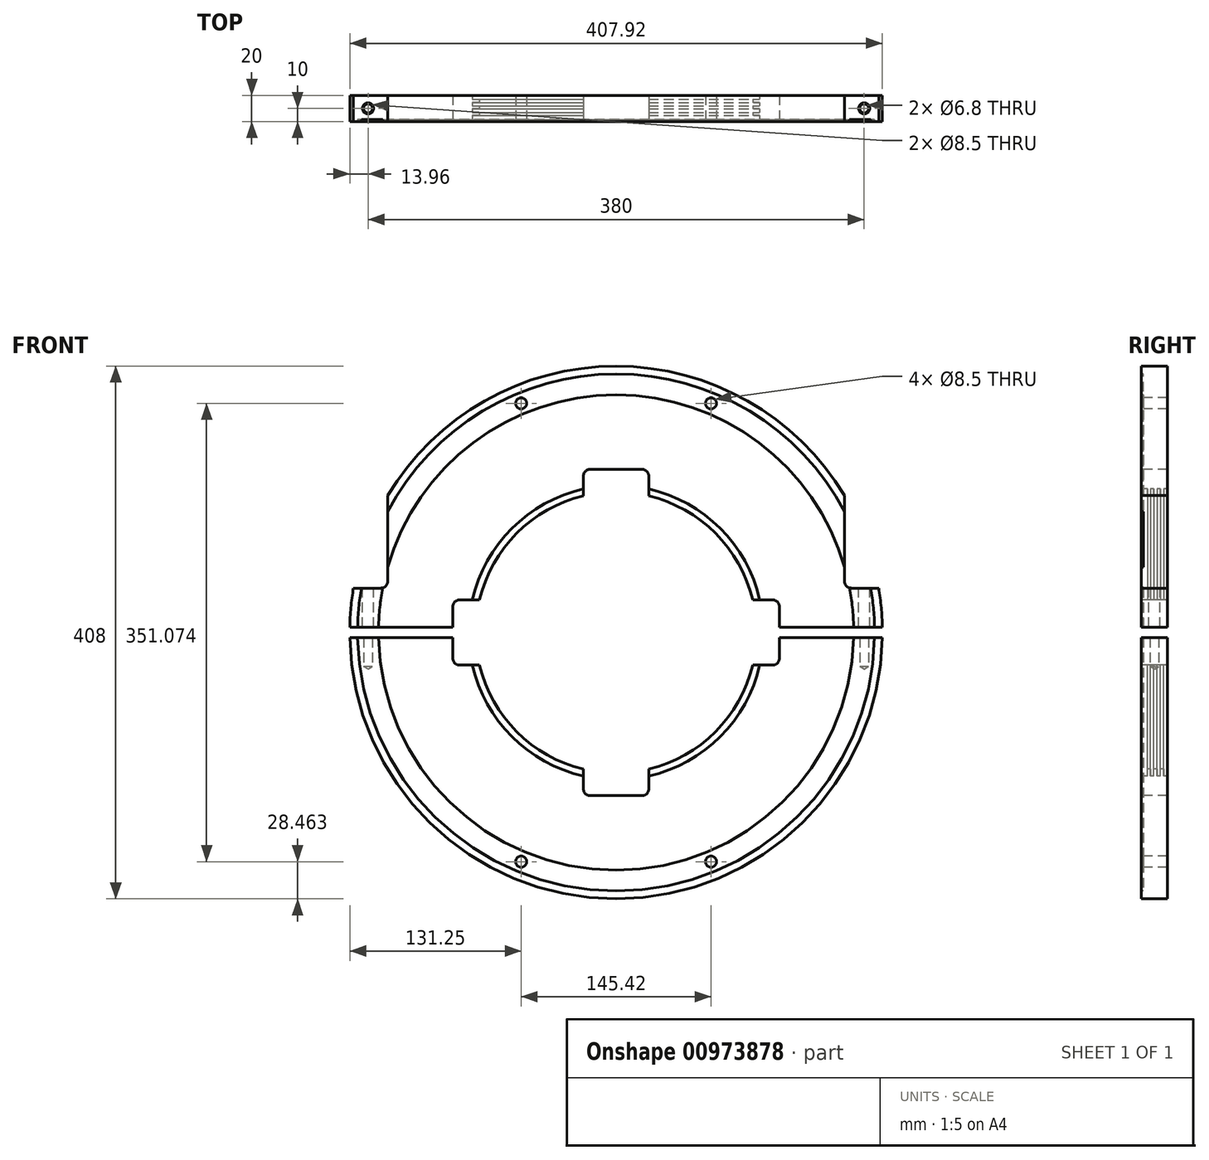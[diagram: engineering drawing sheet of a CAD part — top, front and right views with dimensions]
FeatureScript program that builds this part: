
annotation { "Feature Type Name" : "Feature", "Feature Type Description" : "" }
export const myFeature = defineFeature(function(context is Context, id is Id, definition is map)
    precondition{}
    {
        {
            var Q0;
            Q0=qCreatedBy(makeId("Right.planeOp"),FACE);
            var sketch = newSketch(context, id + "F0", { "sketchPlane" : qUnion([Q0])});
            skLineSegment(sketch, "E0", {"start": v(0, 204) * mm, "end": v(20, 204) * mm});
            skLineSegment(sketch, "E1", {"start": v(0, 204) * mm, "end": v(0, 198) * mm});
            skLineSegment(sketch, "E2", {"start": v(0, 198) * mm, "end": v(1.5, 198) * mm});
            skLineSegment(sketch, "E3", {"start": v(1.5, 198) * mm, "end": v(1.5, 182) * mm});
            skLineSegment(sketch, "E4", {"start": v(1.5, 182) * mm, "end": v(0, 182) * mm});
            skLineSegment(sketch, "E5", {"start": v(0, 182) * mm, "end": v(0, 112.8) * mm});
            skLineSegment(sketch, "E6", {"start": v(0, 112.8) * mm, "end": v(4.6, 112.8) * mm});
            skLineSegment(sketch, "E7", {"start": v(4.6, 112.8) * mm, "end": v(4.6, 107.6) * mm});
            skLineSegment(sketch, "E8", {"start": v(4.6, 107.6) * mm, "end": v(7, 107.6) * mm});
            skLineSegment(sketch, "E9", {"start": v(7, 107.6) * mm, "end": v(7, 112.8) * mm});
            skLineSegment(sketch, "E10", {"start": v(7, 112.8) * mm, "end": v(9.6, 112.8) * mm});
            skLineSegment(sketch, "E11", {"start": v(9.6, 112.8) * mm, "end": v(9.6, 107.6) * mm});
            skLineSegment(sketch, "E12", {"start": v(9.6, 107.6) * mm, "end": v(12, 107.6) * mm});
            skLineSegment(sketch, "E13", {"start": v(12, 107.6) * mm, "end": v(12, 112.8) * mm});
            skLineSegment(sketch, "E14", {"start": v(12, 112.8) * mm, "end": v(14.6, 112.8) * mm});
            skLineSegment(sketch, "E15", {"start": v(14.6, 112.8) * mm, "end": v(14.6, 107.6) * mm});
            skLineSegment(sketch, "E16", {"start": v(14.6, 107.6) * mm, "end": v(17, 107.6) * mm});
            skLineSegment(sketch, "E17", {"start": v(17, 107.6) * mm, "end": v(17, 112.8) * mm});
            skLineSegment(sketch, "E18", {"start": v(17, 112.8) * mm, "end": v(20, 112.8) * mm});
            skLineSegment(sketch, "E19", {"start": v(20, 204) * mm, "end": v(20, 112.8) * mm});
            skPoint(sketch, "E20.orphan", {"position": v(0, 107.6) * mm});
            skLineSegment(sketch, "E21", {"start": v(0, 0) * mm, "end": v(20, 0) * mm, "construction": true});
            skSolve(sketch);
        }
        {
            var Q0;
            Q0 = qSketchRegion(id + "F0", true);
            var Q1;
            Q1=sQuery(id+"F0.wireOp",EDGE,"E21");
            revolve(context, id + "F1", {"surfaceOperationType" : NewSurfaceOperationType.NEW, "entities" : qUnion([Q0]), "axis" : qUnion([Q1]), "revolveType" : RevolveType.FULL});
        }
        {
            var Q0;
            Q0=qCreatedBy(makeId("Front.planeOp"),FACE);
            var sketch = newSketch(context, id + "F2", { "sketchPlane" : qUnion([Q0])});
            skLineSegment(sketch, "E22.bottom", {"start": v(-204, 4) * mm, "end": v(204, 4) * mm});
            skLineSegment(sketch, "E22.top", {"start": v(-204, -4) * mm, "end": v(204, -4) * mm});
            skLineSegment(sketch, "E22.left", {"start": v(-204, 4) * mm, "end": v(-204, -4) * mm});
            skLineSegment(sketch, "E22.right", {"start": v(204, 4) * mm, "end": v(204, -4) * mm});
            skLineSegment(sketch, "E23.bottom", {"start": v(-255, 34) * mm, "end": v(-175, 34) * mm});
            skLineSegment(sketch, "E23.top", {"start": v(-255, 114) * mm, "end": v(-175, 114) * mm});
            skLineSegment(sketch, "E23.left", {"start": v(-255, 34) * mm, "end": v(-255, 114) * mm});
            skLineSegment(sketch, "E23.right", {"start": v(-175, 34) * mm, "end": v(-175, 114) * mm});
            skLineSegment(sketch, "E24.bottom", {"start": v(255, 34) * mm, "end": v(175, 34) * mm});
            skLineSegment(sketch, "E24.top", {"start": v(255, 114) * mm, "end": v(175, 114) * mm});
            skLineSegment(sketch, "E24.left", {"start": v(255, 34) * mm, "end": v(255, 114) * mm});
            skLineSegment(sketch, "E24.right", {"start": v(175, 34) * mm, "end": v(175, 114) * mm});
            skCircle(sketch, "E25", {"center": v(0, 0) * mm, "radius": 190 * mm, "construction": true});
            skLineSegment(sketch, "E26", {"start": v(0, 0) * mm, "end": v(-72.7, 175.54) * mm, "construction": true});
            skLineSegment(sketch, "E27", {"start": v(0, 0) * mm, "end": v(72.7, 175.54) * mm, "construction": true});
            skLineSegment(sketch, "E28", {"start": v(0, 0) * mm, "end": v(-72.7, -175.54) * mm, "construction": true});
            skLineSegment(sketch, "E29", {"start": v(0, 0) * mm, "end": v(72.7, -175.54) * mm, "construction": true});
            skCircle(sketch, "E30", {"center": v(-72.7, 175.54) * mm, "radius": 4.25 * mm});
            skCircle(sketch, "E31", {"center": v(72.7, 175.54) * mm, "radius": 4.25 * mm});
            skCircle(sketch, "E32", {"center": v(-72.7, -175.54) * mm, "radius": 4.25 * mm});
            skCircle(sketch, "E33", {"center": v(72.7, -175.54) * mm, "radius": 4.25 * mm});
            skLineSegment(sketch, "E34.bottom", {"start": v(-25, 125) * mm, "end": v(25, 125) * mm});
            skLineSegment(sketch, "E34.top", {"start": v(-25, -125) * mm, "end": v(25, -125) * mm});
            skLineSegment(sketch, "E34.left", {"start": v(-25, 125) * mm, "end": v(-25, -125) * mm});
            skLineSegment(sketch, "E34.right", {"start": v(25, 125) * mm, "end": v(25, -125) * mm});
            skLineSegment(sketch, "E35.bottom", {"start": v(-125, -25) * mm, "end": v(125, -25) * mm});
            skLineSegment(sketch, "E35.top", {"start": v(-125, 25) * mm, "end": v(125, 25) * mm});
            skLineSegment(sketch, "E35.left", {"start": v(-125, -25) * mm, "end": v(-125, 25) * mm});
            skLineSegment(sketch, "E35.right", {"start": v(125, -25) * mm, "end": v(125, 25) * mm});
            skSolve(sketch);
        }
        {
            var Q0;
            Q0 = qSketchRegion(id + "F2", true);
            extrude(context, id + "F3", {"entities" : qUnion([Q0]), "operationType" : NewBodyOperationType.REMOVE, "oppositeDirection" : true, "depth" : 25 * mm, "offsetDistance" : 25 * mm});
        }
        {
            var Q0;
            Q0=qCreatedBy(makeId("Top.planeOp"),FACE);
            var sketch = newSketch(context, id + "F4", { "sketchPlane" : qUnion([Q0])});
            skLineSegment(sketch, "E36", {"start": v(-190, 10) * mm, "end": v(190, 10) * mm, "construction": true});
            skSolve(sketch);
        }
        {
            var Q0;
            Q0=sQuery(id+"F4.wireOp",VERTEX,"E36.start");
            var Q1;
            Q1=sQuery(id+"F4.wireOp",VERTEX,"E36.end");
            var Q2;
            Q2=makeQuery(id+"F3.boolean.opBoolean","SPLIT",BODY,{"disambiguationData":[OD(0.0)],"derivedFrom":makeQuery(id+"F1.opRevolve","SWEPT_BODY",BODY,{"disambiguationData":[OSD([sQuery(id+"F0.wireOp",EDGE,"E0"),sQuery(id+"F0.wireOp",EDGE,"E1"),sQuery(id+"F0.wireOp",EDGE,"E2"),sQuery(id+"F0.wireOp",EDGE,"E3"),sQuery(id+"F0.wireOp",EDGE,"E4"),sQuery(id+"F0.wireOp",EDGE,"E5"),sQuery(id+"F0.wireOp",EDGE,"E6"),sQuery(id+"F0.wireOp",EDGE,"E7"),sQuery(id+"F0.wireOp",EDGE,"E8"),sQuery(id+"F0.wireOp",EDGE,"E9"),sQuery(id+"F0.wireOp",EDGE,"E10"),sQuery(id+"F0.wireOp",EDGE,"E11"),sQuery(id+"F0.wireOp",EDGE,"E12"),sQuery(id+"F0.wireOp",EDGE,"E13"),sQuery(id+"F0.wireOp",EDGE,"E14"),sQuery(id+"F0.wireOp",EDGE,"E15"),sQuery(id+"F0.wireOp",EDGE,"E16"),sQuery(id+"F0.wireOp",EDGE,"E17"),sQuery(id+"F0.wireOp",EDGE,"E18"),sQuery(id+"F0.wireOp",EDGE,"E19")])]})});
            hole(context, id + "F5", {"style" : HoleStyle.SIMPLE, "endStyle" : HoleEndStyle.BLIND, "standardTappedOrClearance" : lookupTablePath({ "standard" : "ISO", "engagement" : "75%", "pitch" : "1.25 mm", "size" : "M8", "type" : "Tapped" }), "standardBlindInLast" : lookupTablePath({ "standard" : "ISO", "fit" : "Normal", "engagement" : "75%", "pitch" : "1.25 mm", "size" : "M8", "type" : "Clearance & tapped" }), "holeDiameter" : 6.8 * mm, "majorDiameter" : 8 * mm, "showTappedDepth" : true, "holeDepth" : 22 * mm, "tappedDepth" : 17 * mm, "tapClearance" : 4, "locations" : qUnion([Q0, Q1]), "scope" : qUnion([Q2])});
        }
        {
            var Q0;
            Q0=sQuery(id+"F4.wireOp",VERTEX,"E36.start");
            var Q1;
            Q1=sQuery(id+"F4.wireOp",VERTEX,"E36.end");
            var Q2;
            Q2=makeQuery(id+"F3.boolean.opBoolean","SPLIT",BODY,{"disambiguationData":[OD(1.0)],"derivedFrom":makeQuery(id+"F1.opRevolve","SWEPT_BODY",BODY,{"disambiguationData":[OSD([sQuery(id+"F0.wireOp",EDGE,"E0"),sQuery(id+"F0.wireOp",EDGE,"E1"),sQuery(id+"F0.wireOp",EDGE,"E2"),sQuery(id+"F0.wireOp",EDGE,"E3"),sQuery(id+"F0.wireOp",EDGE,"E4"),sQuery(id+"F0.wireOp",EDGE,"E5"),sQuery(id+"F0.wireOp",EDGE,"E6"),sQuery(id+"F0.wireOp",EDGE,"E7"),sQuery(id+"F0.wireOp",EDGE,"E8"),sQuery(id+"F0.wireOp",EDGE,"E9"),sQuery(id+"F0.wireOp",EDGE,"E10"),sQuery(id+"F0.wireOp",EDGE,"E11"),sQuery(id+"F0.wireOp",EDGE,"E12"),sQuery(id+"F0.wireOp",EDGE,"E13"),sQuery(id+"F0.wireOp",EDGE,"E14"),sQuery(id+"F0.wireOp",EDGE,"E15"),sQuery(id+"F0.wireOp",EDGE,"E16"),sQuery(id+"F0.wireOp",EDGE,"E17"),sQuery(id+"F0.wireOp",EDGE,"E18"),sQuery(id+"F0.wireOp",EDGE,"E19")])]})});
            hole(context, id + "F6", {"style" : HoleStyle.SIMPLE, "endStyle" : HoleEndStyle.THROUGH, "oppositeDirection" : true, "holeDiameter" : 8.5 * mm, "majorDiameter" : 8 * mm, "tappedDepth" : 16 * mm, "tapClearance" : 5, "locations" : qUnion([Q0, Q1]), "scope" : qUnion([Q2])});
        }
        {
            var Q0;
            Q0=makeQuery(id+"F3.boolean.opBoolean","COPY",EDGE,{"derivedFrom":makeQuery(id+"F3.opExtrude","SWEPT_EDGE",EDGE,{"disambiguationData":[OSD([sQuery(id+"F2.wireOp",EDGE,"E35.bottom"),sQuery(id+"F2.wireOp",EDGE,"E35.left")])]})});
            var Q1;
            Q1=makeQuery(id+"F3.boolean.opBoolean","COPY",EDGE,{"derivedFrom":makeQuery(id+"F3.opExtrude","SWEPT_EDGE",EDGE,{"disambiguationData":[OSD([sQuery(id+"F2.wireOp",EDGE,"E35.top"),sQuery(id+"F2.wireOp",EDGE,"E35.left")])]})});
            var Q2;
            Q2=makeQuery(id+"F3.boolean.opBoolean","COPY",EDGE,{"derivedFrom":makeQuery(id+"F3.opExtrude","SWEPT_EDGE",EDGE,{"disambiguationData":[OSD([sQuery(id+"F2.wireOp",EDGE,"E34.bottom"),sQuery(id+"F2.wireOp",EDGE,"E34.left")])]})});
            var Q3;
            Q3=makeQuery(id+"F3.boolean.opBoolean","COPY",EDGE,{"derivedFrom":makeQuery(id+"F3.opExtrude","SWEPT_EDGE",EDGE,{"disambiguationData":[OSD([sQuery(id+"F2.wireOp",EDGE,"E34.bottom"),sQuery(id+"F2.wireOp",EDGE,"E34.right")])]})});
            var Q4;
            Q4=makeQuery(id+"F3.boolean.opBoolean","COPY",EDGE,{"derivedFrom":makeQuery(id+"F3.opExtrude","SWEPT_EDGE",EDGE,{"disambiguationData":[OSD([sQuery(id+"F2.wireOp",EDGE,"E35.top"),sQuery(id+"F2.wireOp",EDGE,"E35.right")])]})});
            var Q5;
            Q5=makeQuery(id+"F3.boolean.opBoolean","COPY",EDGE,{"derivedFrom":makeQuery(id+"F3.opExtrude","SWEPT_EDGE",EDGE,{"disambiguationData":[OSD([sQuery(id+"F2.wireOp",EDGE,"E35.bottom"),sQuery(id+"F2.wireOp",EDGE,"E35.right")])]})});
            var Q6;
            Q6=makeQuery(id+"F3.boolean.opBoolean","COPY",EDGE,{"derivedFrom":makeQuery(id+"F3.opExtrude","SWEPT_EDGE",EDGE,{"disambiguationData":[OSD([sQuery(id+"F2.wireOp",EDGE,"E34.top"),sQuery(id+"F2.wireOp",EDGE,"E34.right")])]})});
            var Q7;
            Q7=makeQuery(id+"F3.boolean.opBoolean","COPY",EDGE,{"derivedFrom":makeQuery(id+"F3.opExtrude","SWEPT_EDGE",EDGE,{"disambiguationData":[OSD([sQuery(id+"F2.wireOp",EDGE,"E34.top"),sQuery(id+"F2.wireOp",EDGE,"E34.left")])]})});
            var Q8;
            Q8=makeQuery(id+"F3.boolean.opBoolean","COPY",EDGE,{"derivedFrom":makeQuery(id+"F3.opExtrude","SWEPT_EDGE",EDGE,{"disambiguationData":[OSD([sQuery(id+"F2.wireOp",EDGE,"E23.bottom"),sQuery(id+"F2.wireOp",EDGE,"E23.right")])]})});
            var Q9;
            Q9=makeQuery(id+"F3.boolean.opBoolean","COPY",EDGE,{"derivedFrom":makeQuery(id+"F3.opExtrude","SWEPT_EDGE",EDGE,{"disambiguationData":[OSD([sQuery(id+"F2.wireOp",EDGE,"E24.bottom"),sQuery(id+"F2.wireOp",EDGE,"E24.right")])]})});
            fillet(context, id + "F7", {"entities" : qUnion([Q0, Q1, Q2, Q3, Q4, Q5, Q6, Q7, Q8, Q9]), "radius" : 5 * mm, "tangentPropagation" : true, "allowEdgeOverflow" : false});
        }
    });
